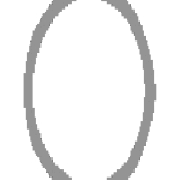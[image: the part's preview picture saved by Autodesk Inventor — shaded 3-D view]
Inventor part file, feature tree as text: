
AUTODESK INVENTOR PART (.ipt)
format: ipt  version: 2021 (Build 250183000, 183)  size: 160,256 bytes
history: native  units: in
note: dims shown in document units (in); Inventor stores cm internally (conversion verified against a paired STEP export)
features: other x5, sketch x2, sweep x1, plane x1
ambient origin geometry x8: Origin, YZ Plane, XZ Plane, XY Plane, X Axis, Y Axis, Z Axis, Center Point
bodies: Solid1 (feature_tree), Body (feature_tree)
feature tree (9):
  other  "Driven Length"
  other  "Frame Generator"
  other  "Start Plane"
  other  "End Plane"
  sweep  "Sweep Path"
  other  "Orientation Work Plane"
  sketch  "Sketch2"  dims[d0=1.0in d1=0.065in]
  plane  "Work Plane3"
  sketch  "Sketch3"  dims[d2=7.854in d4=-0.0in d5=7.854in d8=90.0deg d9=7.854in d10=0.0in d11=0.0in]
